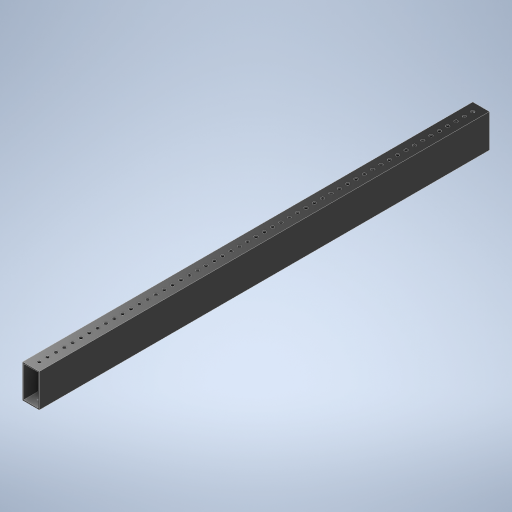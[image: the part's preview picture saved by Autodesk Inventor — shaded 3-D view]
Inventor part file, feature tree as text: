
AUTODESK INVENTOR PART (.ipt)
format: ipt  version: 2024.2 (Build 282272000, 272)  size: 790,528 bytes
history: native  units: in
note: dims shown in document units (in); Inventor stores cm internally (conversion verified against a paired STEP export)
features: other x13, extrude x10, hole x3, pattern_linear x3, mirror x3, sheet_metal_op x1, plane x1, sketch x1
ambient origin geometry x8: Origin, YZ Plane, XZ Plane, XY Plane, X Axis, Y Axis, Z Axis, Center Point
bodies: Solid1 (feature_tree)
feature tree (35):
  other  "Blocks"
  other  "Base Sketch"
  extrude  "Base"  Depth=1.0in
  extrude  "MAX Corner"  Depth=0.0625in
  extrude  "MAX Corner Cut"  Depth=0.0625in
  extrude  "Scribe Lines"  Depth=1.0in
  other  "Side Middle"
  other  "Top Middle"
  other  "Side Holes Sketch"
  hole  "Top Side Hole"  [1 undecoded]
  hole  "Mid Side Hole"  [1 undecoded]
  hole  "Btm Side Hole"  [1 undecoded]
  pattern_linear  "Side Holes"  Spacing1=0.04in  [1 undecoded]
  mirror  "Side Mirror"
  extrude  "MAXTube Hole"  Depth=27.0in
  extrude  "MAXTube Outside"  TaperAngle=0.0deg  [1 undecoded]
  pattern_linear  "MAXTube Pattern"  Spacing1=27.0in  [1 undecoded]
  mirror  "MAXTube Mirror"
  extrude  "Left Top Hole"  TaperAngle=0.0deg  [1 undecoded]
  extrude  "Mid Top Hole"  TaperAngle=0.0deg  [1 undecoded]
  extrude  "Right Top Hole"  Depth=1.0in
  pattern_linear  "Top Holes"  Spacing1=0.0in  [1 undecoded]
  mirror  "Top Mirror"
  extrude  "Extrusion11"  Depth=1.0in
  sheet_metal_op  "Corner"
  other  "MAXTube"
  plane  "Work Plane3"
  sketch  "Sketch5"  dims[d0=2.0in d1=1.0in d2=0.0625in d3=0.0625in d4=0.4375in d5=0.04in d6=0.0671in d7=0.0272in d8=0.0in d9=0.0in d10=0.0in d11=0.085in d12=0.085in d16=0.04in d17=0.04in d18=0.04in d19=0.04in d20=27.0in d21=0.0in d22=27.0in d23=0.0in d24=0.0in d25=0.0in d26=0.005in d30=0.0in d31=0.0in d34=0.5in d35=0.5in d38=0.5in d40=0.196in d41=0.75in d42=0.375in d43=0.25in d44=0.5635in d45=1.0in d46=0.8108in d47=0.196in d48=0.75in d49=0.375in d50=0.25in d51=0.5635in d52=1.0in d53=0.8108in d54=0.196in d55=0.75in d56=0.375in d57=0.25in d58=0.5635in d59=1.0in d60=0.8108in d61=0.5in d62=0.3937in d64=0.5in d69=1.5in d70=0.0in d71=0.0in d72=2.7559in d74=2.0in d78=2.0in d79=-13.5in d80=0.196in d81=0.0in d82=0.0in d83=0.5in d84=0.0in d85=0.0in d86=0.0in d87=0.0in d88=0.0in d89=0.0in d90=10.6299in d92=0.5in d93=1.0in d95=0.0in d96=0.0in d97=1.5in d98=24.0in d100=-13.5in d101=0.25in d102=0.25in d103=0.25in d104=0.25in d105=0.25in d106=0.25in d107=0.25in d108=0.25in d109=0.5in d110=0.0in]
  other  "Corner:5"
  other  "Corner:6"
  other  "Corner:7"
  other  "Corner:8"
  other  "MAXTube:1"
  other  "MAXTube:2"
  other  "MAXTube:3"
note: 9 required parameter values undecoded (feature->parameter linkage not recoverable at this tier; creation-order binding heuristic only, values carry confidence <= 0.55)
